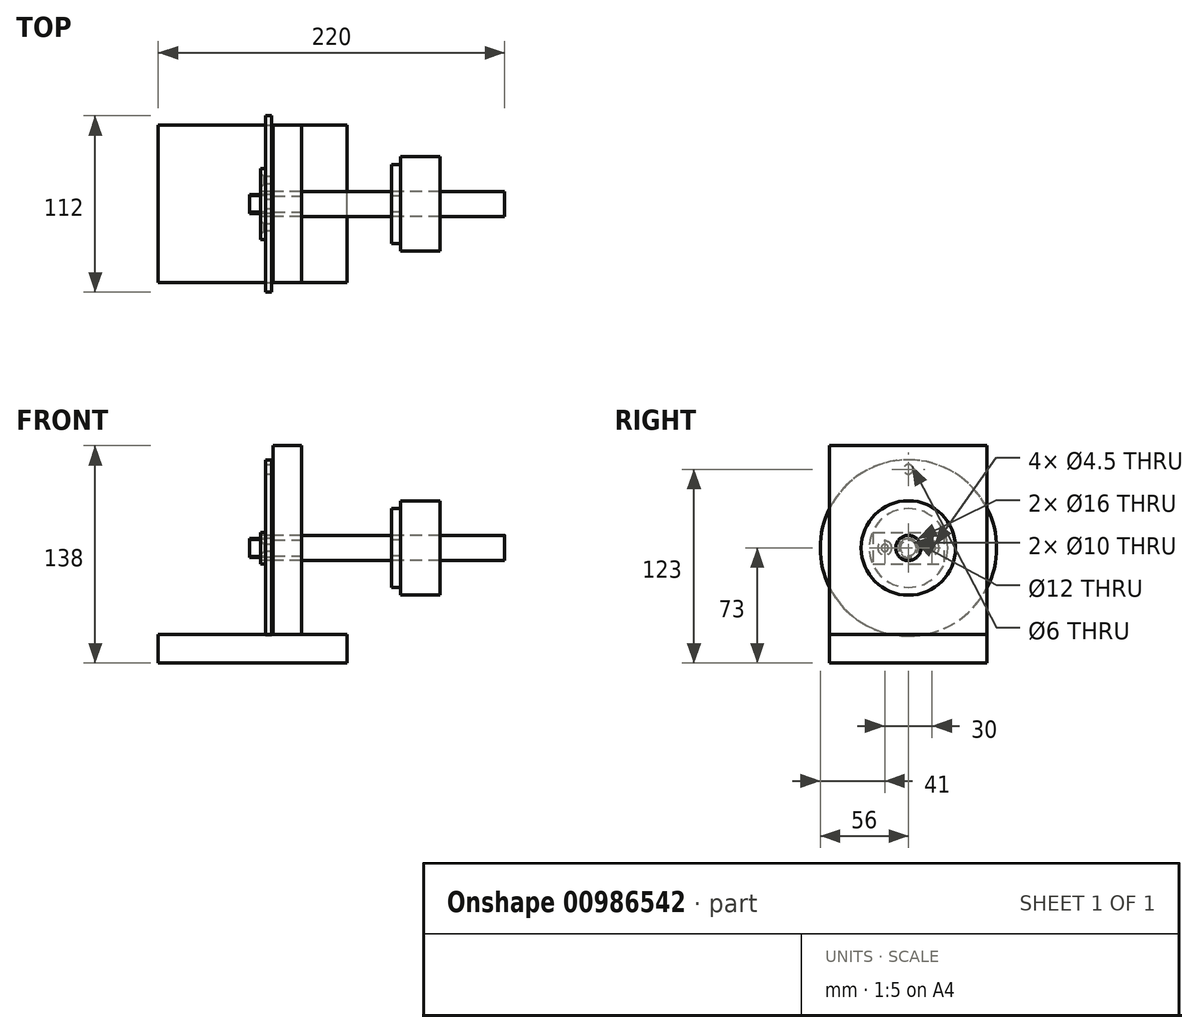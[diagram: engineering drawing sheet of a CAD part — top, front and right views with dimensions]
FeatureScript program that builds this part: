
annotation { "Feature Type Name" : "Feature", "Feature Type Description" : "" }
export const myFeature = defineFeature(function(context is Context, id is Id, definition is map)
    precondition{}
    {
        {
            var Q0;
            Q0=qCreatedBy(makeId("Right.planeOp"),FACE);
            var sketch = newSketch(context, id + "F0", { "sketchPlane" : qUnion([Q0])});
            skCircle(sketch, "E0", {"center": v(0, 0) * mm, "radius": 56 * mm});
            skCircle(sketch, "E1", {"center": v(0, 0) * mm, "radius": 6 * mm});
            skSolve(sketch);
        }
        {
            var Q0;
            Q0 = qSketchRegion(id + "F0", true);
            extrude(context, id + "F1", {"entities" : qUnion([Q0]), "depth" : 2 * mm, "offsetDistance" : 25 * mm, "hasSecondDirection" : true, "secondDirectionOppositeDirection" : true, "secondDirectionDepth" : 2 * mm});
        }
        {
            var Q0;
            Q0=makeQuery(id+"F1.opExtrude","CAP_FACE",FACE,{"disambiguationData":[OSD([sQuery(id+"F0.wireOp",EDGE,"E0")])],"isStart":false});
            var sketch = newSketch(context, id + "F2", { "sketchPlane" : qUnion([Q0])});
            skCircle(sketch, "E2", {"center": v(0, 50) * mm, "radius": 3 * mm});
            skSolve(sketch);
        }
        {
            var Q0;
            Q0 = qSketchRegion(id + "F2", true);
            extrude(context, id + "F3", {"entities" : qUnion([Q0]), "operationType" : NewBodyOperationType.REMOVE, "endBound" : BoundingType.THROUGH_ALL, "oppositeDirection" : true, "depth" : 25 * mm, "offsetDistance" : 25 * mm});
        }
        {
            var Q0;
            Q0=qCreatedBy(makeId("Front.planeOp"),FACE);
            var sketch = newSketch(context, id + "F4", { "sketchPlane" : qUnion([Q0])});
            skLineSegment(sketch, "E3.bottom", {"start": v(-70, -73) * mm, "end": v(50, -73) * mm});
            skLineSegment(sketch, "E3.top", {"start": v(-70, -55) * mm, "end": v(50, -55) * mm});
            skLineSegment(sketch, "E3.left", {"start": v(-70, -73) * mm, "end": v(-70, -55) * mm});
            skLineSegment(sketch, "E3.right", {"start": v(50, -73) * mm, "end": v(50, -55) * mm});
            skSolve(sketch);
        }
        {
            var Q0;
            Q0 = qSketchRegion(id + "F4", true);
            extrude(context, id + "F5", {"entities" : qUnion([Q0]), "depth" : 50 * mm, "offsetDistance" : 25 * mm, "hasSecondDirection" : true, "secondDirectionOppositeDirection" : true, "secondDirectionDepth" : 50 * mm});
        }
        {
            var Q0;
            Q0=makeQuery(id+"F5.opExtrude","SWEPT_FACE",FACE,{"disambiguationData":[OSD([sQuery(id+"F4.wireOp",EDGE,"E3.top")])]});
            var sketch = newSketch(context, id + "F6", { "sketchPlane" : qUnion([Q0])});
            skLineSegment(sketch, "E4.bottom", {"start": v(3, 50) * mm, "end": v(21, 50) * mm});
            skLineSegment(sketch, "E4.top", {"start": v(3, -50) * mm, "end": v(21, -50) * mm});
            skLineSegment(sketch, "E4.left", {"start": v(3, 50) * mm, "end": v(3, -50) * mm});
            skLineSegment(sketch, "E4.right", {"start": v(21, 50) * mm, "end": v(21, -50) * mm});
            skSolve(sketch);
        }
        {
            var Q0;
            Q0 = qSketchRegion(id + "F6", true);
            extrude(context, id + "F7", {"entities" : qUnion([Q0]), "depth" : 120 * mm, "offsetDistance" : 25 * mm});
        }
        {
            var Q0;
            Q0=makeQuery(id+"F7.opExtrude","SWEPT_FACE",FACE,{"disambiguationData":[OSD([sQuery(id+"F6.wireOp",EDGE,"E4.right")])]});
            var sketch = newSketch(context, id + "F8", { "sketchPlane" : qUnion([Q0])});
            skCircle(sketch, "E5", {"center": v(0, 0) * mm, "radius": 5 * mm});
            skSolve(sketch);
        }
        {
            var Q0;
            Q0 = qSketchRegion(id + "F8", true);
            extrude(context, id + "F9", {"entities" : qUnion([Q0]), "operationType" : NewBodyOperationType.REMOVE, "endBound" : BoundingType.THROUGH_ALL, "oppositeDirection" : true, "depth" : 25 * mm, "offsetDistance" : 25 * mm});
        }
        {
            var Q0;
            Q0=qCreatedBy(makeId("Right.planeOp"),FACE);
            var sketch = newSketch(context, id + "F10", { "sketchPlane" : qUnion([Q0])});
            skCircle(sketch, "E6", {"center": v(0, 0) * mm, "radius": 8 * mm});
            skSolve(sketch);
        }
        {
            var Q0;
            Q0 = qSketchRegion(id + "F10", true);
            extrude(context, id + "F11", {"entities" : qUnion([Q0]), "depth" : 150 * mm, "offsetDistance" : 25 * mm, "hasSecondDirection" : true, "secondDirectionOppositeDirection" : true, "secondDirectionDepth" : 12 * mm});
        }
        {
            var Q0;
            Q0=makeQuery(id+"F1.opExtrude","CAP_FACE",FACE,{"disambiguationData":[OSD([sQuery(id+"F0.wireOp",EDGE,"E0"),sQuery(id+"F0.wireOp",EDGE,"E1")])],"isStart":true});
            var sketch = newSketch(context, id + "F12", { "sketchPlane" : qUnion([Q0])});
            skPoint(sketch, "E7", {"position": v(15, 0) * mm});
            skPoint(sketch, "E8", {"position": v(-15, 0) * mm});
            skSolve(sketch);
        }
        {
            var Q0;
            Q0=sQuery(id+"F12.wireOp",VERTEX,"E8");
            var Q1;
            Q1=sQuery(id+"F12.wireOp",VERTEX,"E7");
            var Q2;
            Q2=makeQuery(id+"F1.opExtrude","SWEPT_BODY",BODY,{"disambiguationData":[OSD([sQuery(id+"F0.wireOp",EDGE,"E0"),sQuery(id+"F0.wireOp",EDGE,"E1")])]});
            hole(context, id + "F13", {"style" : HoleStyle.SIMPLE, "endStyle" : HoleEndStyle.THROUGH, "standardTappedOrClearance" : lookupTablePath({ "fit" : "Normal", "standard" : "ISO", "size" : "M4", "type" : "Clearance" }), "standardBlindInLast" : lookupTablePath({ "fit" : "Normal", "standard" : "ISO", "engagement" : "75%", "pitch" : "0.7 mm", "size" : "M4", "type" : "Clearance & tapped" }), "holeDiameter" : 4.5 * mm, "majorDiameter" : 4 * mm, "isTappedThrough" : true, "tappedDepth" : 16 * mm, "tapClearance" : 3, "locations" : qUnion([Q0, Q1]), "scope" : qUnion([Q2])});
        }
        {
            var Q0;
            Q0=makeQuery(id+"F1.opExtrude","CAP_FACE",FACE,{"disambiguationData":[OSD([sQuery(id+"F0.wireOp",EDGE,"E0"),sQuery(id+"F0.wireOp",EDGE,"E1")])],"isStart":true});
            var sketch = newSketch(context, id + "F14", { "sketchPlane" : qUnion([Q0])});
            skLineSegment(sketch, "E9.bottom", {"start": v(22.5, 10) * mm, "end": v(-22.5, 10) * mm});
            skLineSegment(sketch, "E9.top", {"start": v(22.5, -10) * mm, "end": v(-22.5, -10) * mm});
            skLineSegment(sketch, "E9.left", {"start": v(22.5, 10) * mm, "end": v(22.5, -10) * mm});
            skLineSegment(sketch, "E9.right", {"start": v(-22.5, 10) * mm, "end": v(-22.5, -10) * mm});
            skPoint(sketch, "E9.middle", {"position": v(0, 0) * mm});
            skSolve(sketch);
        }
        {
            var Q0;
            Q0 = qSketchRegion(id + "F14", true);
            extrude(context, id + "F15", {"entities" : qUnion([Q0]), "depth" : 3 * mm, "offsetDistance" : 25 * mm});
        }
        {
            var Q0;
            Q0=makeQuery(id+"F15.opExtrude","CAP_FACE",FACE,{"disambiguationData":[OSD([sQuery(id+"F14.wireOp",EDGE,"E9.bottom"),sQuery(id+"F14.wireOp",EDGE,"E9.top"),sQuery(id+"F14.wireOp",EDGE,"E9.left"),sQuery(id+"F14.wireOp",EDGE,"E9.right")])],"isStart":false});
            var sketch = newSketch(context, id + "F16", { "sketchPlane" : qUnion([Q0])});
            skPoint(sketch, "E10", {"position": v(0, 0) * mm});
            skPoint(sketch, "E11", {"position": v(15, 0) * mm});
            skPoint(sketch, "E12", {"position": v(-15, 0) * mm});
            skCircle(sketch, "E13.0", {"center": v(15, 0) * mm, "radius": 2.25 * mm});
            skCircle(sketch, "E13.1", {"center": v(-15, 0) * mm, "radius": 2.25 * mm});
            skSolve(sketch);
        }
        {
            var Q0;
            Q0=sQuery(id+"F16.wireOp",VERTEX,"E12");
            var Q1;
            Q1=sQuery(id+"F16.wireOp",VERTEX,"E11");
            var Q2;
            Q2=makeQuery(id+"F15.opExtrude","SWEPT_BODY",BODY,{"disambiguationData":[OSD([sQuery(id+"F14.wireOp",EDGE,"E9.bottom"),sQuery(id+"F14.wireOp",EDGE,"E9.top"),sQuery(id+"F14.wireOp",EDGE,"E9.left"),sQuery(id+"F14.wireOp",EDGE,"E9.right")])]});
            hole(context, id + "F17", {"style" : HoleStyle.C_SINK, "endStyle" : HoleEndStyle.THROUGH, "standardTappedOrClearance" : lookupTablePath({ "fit" : "Normal", "standard" : "ISO", "size" : "M4", "type" : "Clearance" }), "standardBlindInLast" : lookupTablePath({ "fit" : "Normal", "standard" : "ISO", "engagement" : "75%", "pitch" : "0.7 mm", "size" : "M4", "type" : "Clearance & tapped" }), "holeDiameter" : 4.5 * mm, "cSinkDiameter" : 8.96 * mm, "cSinkAngle" : 90 * degree, "majorDiameter" : 5 * mm, "isTappedThrough" : true, "tappedDepth" : 16 * mm, "tapClearance" : 3, "locations" : qUnion([Q0, Q1]), "scope" : qUnion([Q2])});
        }
        {
            var Q0;
            Q0=sQuery(id+"F16.wireOp",VERTEX,"E10");
            var Q1;
            Q1=makeQuery(id+"F15.opExtrude","SWEPT_BODY",BODY,{"disambiguationData":[OSD([sQuery(id+"F14.wireOp",EDGE,"E9.bottom"),sQuery(id+"F14.wireOp",EDGE,"E9.top"),sQuery(id+"F14.wireOp",EDGE,"E9.left"),sQuery(id+"F14.wireOp",EDGE,"E9.right")])]});
            hole(context, id + "F18", {"style" : HoleStyle.SIMPLE, "endStyle" : HoleEndStyle.THROUGH, "holeDiameter" : 16 * mm, "majorDiameter" : 10 * mm, "isTappedThrough" : true, "tappedDepth" : 16 * mm, "tapClearance" : 3, "locations" : qUnion([Q0]), "scope" : qUnion([Q1])});
        }
        {
            var Q0;
            Q0=qCreatedBy(makeId("Front.planeOp"),FACE);
            var sketch = newSketch(context, id + "F19", { "sketchPlane" : qUnion([Q0])});
            skLineSegment(sketch, "E14", {"start": v(81, 0) * mm, "end": v(81, 88.8) * mm, "construction": true});
            skLineSegment(sketch, "E15", {"start": v(81, 0) * mm, "end": v(304.17, 0) * mm, "construction": true});
            skLineSegment(sketch, "E16", {"start": v(84, 5) * mm, "end": v(84, 25) * mm});
            skLineSegment(sketch, "E17", {"start": v(84, 25) * mm, "end": v(81, 25) * mm});
            skLineSegment(sketch, "E18", {"start": v(84, 5) * mm, "end": v(81, 5) * mm});
            skLineSegment(sketch, "E19.MirrorCS", {"start": v(78, 5) * mm, "end": v(81, 5) * mm});
            skLineSegment(sketch, "E20.MirrorCS", {"start": v(78, 5) * mm, "end": v(78, 25) * mm});
            skLineSegment(sketch, "E21.MirrorCS", {"start": v(78, 25) * mm, "end": v(81, 25) * mm});
            skSolve(sketch);
        }
        {
            var Q0;
            Q0 = qSketchRegion(id + "F19", true);
            var Q1;
            Q1=sQuery(id+"F19.wireOp",EDGE,"E15");
            revolve(context, id + "F20", {"surfaceOperationType" : NewSurfaceOperationType.NEW, "entities" : qUnion([Q0]), "axis" : qUnion([Q1]), "revolveType" : RevolveType.FULL});
        }
        {
            var Q0;
            Q0=makeQuery(id+"F20.opRevolve","SWEPT_FACE",FACE,{"disambiguationData":[OSD([sQuery(id+"F19.wireOp",EDGE,"E16")])]});
            var sketch = newSketch(context, id + "F21", { "sketchPlane" : qUnion([Q0])});
            skCircle(sketch, "E22", {"center": v(0, 0) * mm, "radius": 30 * mm});
            skCircle(sketch, "E23.0", {"center": v(0, 0) * mm, "radius": 8 * mm});
            skSolve(sketch);
        }
        {
            var Q0;
            Q0 = qSketchRegion(id + "F21", true);
            extrude(context, id + "F22", {"entities" : qUnion([Q0]), "depth" : 25 * mm, "offsetDistance" : 25 * mm});
        }
        {
            var Q0;
            Q0=makeQuery(id+"F11.opExtrude","CAP_FACE",FACE,{"disambiguationData":[OSD([sQuery(id+"F10.wireOp",EDGE,"E6")])],"isStart":true});
            var sketch = newSketch(context, id + "F23", { "sketchPlane" : qUnion([Q0])});
            skLineSegment(sketch, "E24.bottom", {"start": v(6, 6) * mm, "end": v(-6, 6) * mm});
            skLineSegment(sketch, "E24.top", {"start": v(6, -6) * mm, "end": v(-6, -6) * mm});
            skLineSegment(sketch, "E24.left", {"start": v(6, 6) * mm, "end": v(6, -6) * mm});
            skLineSegment(sketch, "E24.right", {"start": v(-6, 6) * mm, "end": v(-6, -6) * mm});
            skPoint(sketch, "E24.middle", {"position": v(0, 0) * mm});
            skSolve(sketch);
        }
        {
            var Q0;
            {var subQ0=sQuery(id+"F23.wireOp",EDGE,"E24.bottom");var subQ1=makeQuery(id+"F11.opExtrude","CAP_EDGE",EDGE,{"disambiguationData":[OSD([sQuery(id+"F10.wireOp",EDGE,"E6")])],"isStart":true});var subQ2=makeQuery(id+"F23.imprint","INTERSECT",VERTEX,{"disambiguationData":[OD(0.0)],"derivedFrom":[subQ1,subQ0]});Q0=makeQuery(id+"F23.imprint","IMPRINT",FACE,{"disambiguationData":[TD([[makeQuery(id+"F23.imprint","IMPRINT",EDGE,{"disambiguationData":[TD([[subQ2,-1.0]])],"derivedFrom":subQ0}),-1.0]])]});}
            var Q1;
            {var subQ0=sQuery(id+"F23.wireOp",EDGE,"E24.left");var subQ1=makeQuery(id+"F11.opExtrude","CAP_EDGE",EDGE,{"disambiguationData":[OSD([sQuery(id+"F10.wireOp",EDGE,"E6")])],"isStart":true});var subQ2=makeQuery(id+"F23.imprint","INTERSECT",VERTEX,{"disambiguationData":[OD(0.0)],"derivedFrom":[subQ1,subQ0]});Q1=makeQuery(id+"F23.imprint","IMPRINT",FACE,{"disambiguationData":[TD([[makeQuery(id+"F23.imprint","IMPRINT",EDGE,{"disambiguationData":[TD([[subQ2,-1.0]])],"derivedFrom":subQ0}),1.0]])]});}
            var Q2;
            {var subQ0=sQuery(id+"F23.wireOp",EDGE,"E24.top");var subQ1=makeQuery(id+"F11.opExtrude","CAP_EDGE",EDGE,{"disambiguationData":[OSD([sQuery(id+"F10.wireOp",EDGE,"E6")])],"isStart":true});var subQ2=makeQuery(id+"F23.imprint","INTERSECT",VERTEX,{"disambiguationData":[OD(0.0)],"derivedFrom":[subQ1,subQ0]});Q2=makeQuery(id+"F23.imprint","IMPRINT",FACE,{"disambiguationData":[TD([[makeQuery(id+"F23.imprint","IMPRINT",EDGE,{"disambiguationData":[TD([[subQ2,-1.0]])],"derivedFrom":subQ0}),1.0]])]});}
            var Q3;
            {var subQ0=sQuery(id+"F23.wireOp",EDGE,"E24.right");var subQ1=makeQuery(id+"F11.opExtrude","CAP_EDGE",EDGE,{"disambiguationData":[OSD([sQuery(id+"F10.wireOp",EDGE,"E6")])],"isStart":true});var subQ2=makeQuery(id+"F23.imprint","INTERSECT",VERTEX,{"disambiguationData":[OD(0.0)],"derivedFrom":[subQ1,subQ0]});Q3=makeQuery(id+"F23.imprint","IMPRINT",FACE,{"disambiguationData":[TD([[makeQuery(id+"F23.imprint","IMPRINT",EDGE,{"disambiguationData":[TD([[subQ2,-1.0]])],"derivedFrom":subQ0}),-1.0]])]});}
            extrude(context, id + "F24", {"entities" : qUnion([Q0, Q1, Q2, Q3]), "operationType" : NewBodyOperationType.REMOVE, "oppositeDirection" : true, "depth" : 10 * mm, "offsetDistance" : 25 * mm});
        }
    });
